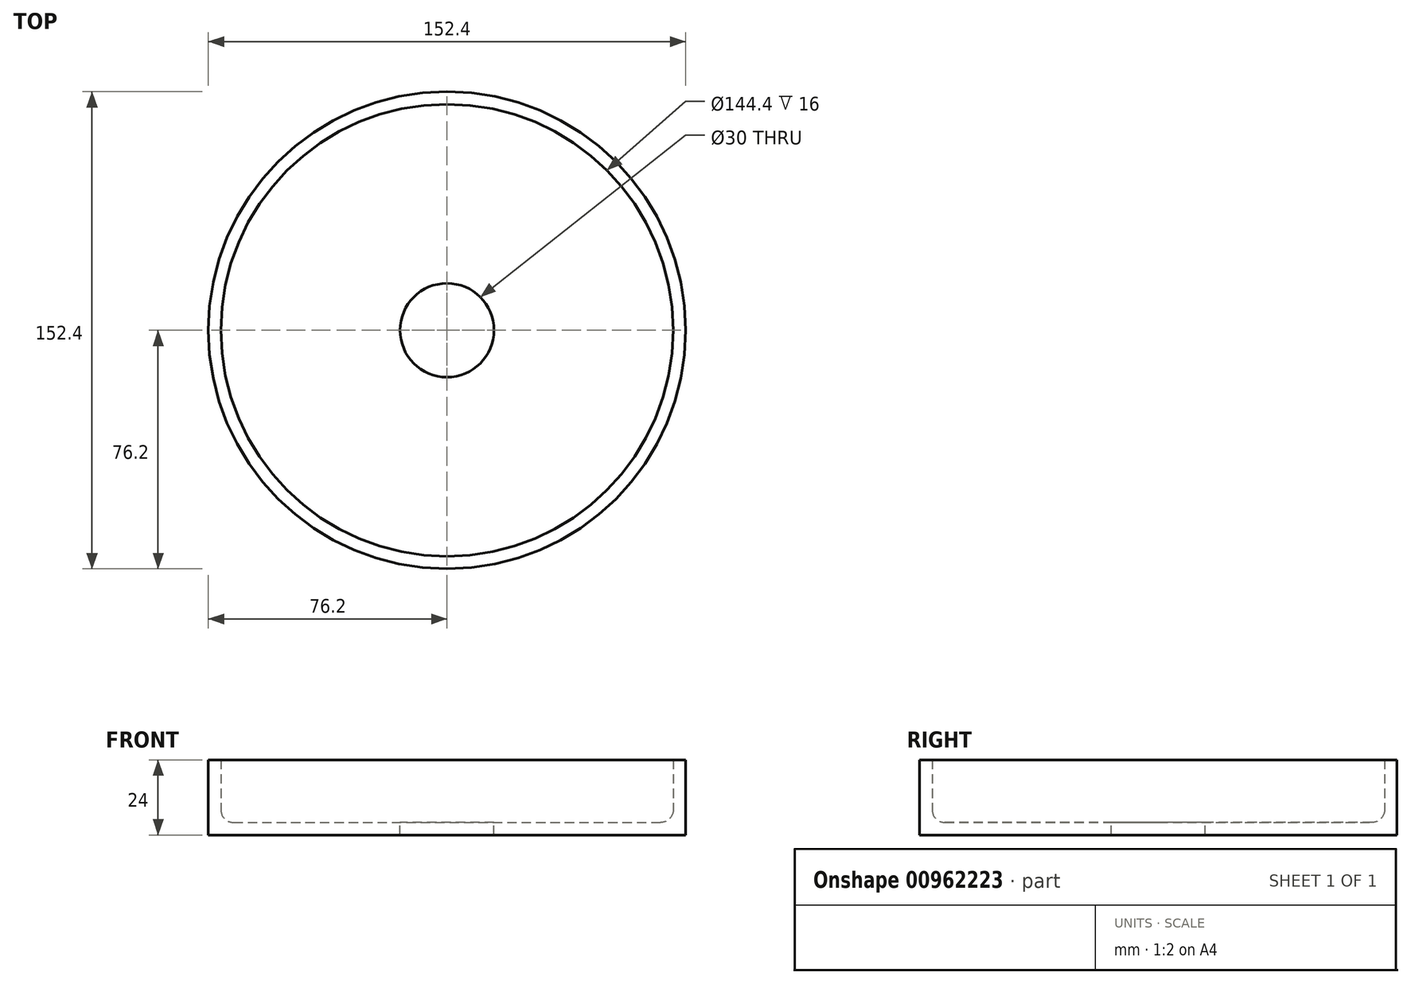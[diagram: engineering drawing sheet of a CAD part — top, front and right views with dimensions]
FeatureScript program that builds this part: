
annotation { "Feature Type Name" : "Feature", "Feature Type Description" : "" }
export const myFeature = defineFeature(function(context is Context, id is Id, definition is map)
    precondition{}
    {
        {
            var Q0;
            Q0=qCreatedBy(makeId("Front.planeOp"),FACE);
            var sketch = newSketch(context, id + "F0", { "sketchPlane" : qUnion([Q0])});
            skLineSegment(sketch, "E0", {"start": v(0, 0) * mm, "end": v(0, 4) * mm});
            skLineSegment(sketch, "E1.bottom", {"start": v(0, 0) * mm, "end": v(76.2, 0) * mm});
            skLineSegment(sketch, "E1.top", {"start": v(0, 4) * mm, "end": v(68.2, 4) * mm});
            skLineSegment(sketch, "E1.right", {"start": v(76.2, 0) * mm, "end": v(76.2, 4) * mm});
            skLineSegment(sketch, "E2.0", {"start": v(72.2, 0) * mm, "end": v(72.2, 3) * mm});
            skLineSegment(sketch, "E3.0", {"start": v(0, 20) * mm, "end": v(33.38, 20) * mm});
            skPoint(sketch, "E4.oppositeSnap0", {"position": v(72.2, 1.5) * mm});
            skLineSegment(sketch, "E4.bottom", {"start": v(76.2, 4) * mm, "end": v(72.2, 4) * mm});
            skLineSegment(sketch, "E4.top", {"start": v(76.2, 24) * mm, "end": v(72.2, 24) * mm});
            skLineSegment(sketch, "E4.left", {"start": v(76.2, 4) * mm, "end": v(76.2, 24) * mm});
            skLineSegment(sketch, "E4.right", {"start": v(72.2, 8) * mm, "end": v(72.2, 24) * mm});
            skPoint(sketch, "E5.newPointB", {"position": v(76.2, 4) * mm});
            skArc(sketch, "E5.filletArc", {"start": v(68.2, 4) * mm, "mid": v(71.03, 5.17) * mm, "end": v(72.2, 8) * mm});
            skSolve(sketch);
        }
        {
            var Q0;
            Q0=makeQuery(id+"F0.imprint","IMPRINT",FACE,{"disambiguationData":[TD([[makeQuery(id+"F0.imprint","IMPRINT",EDGE,{"derivedFrom":sQuery(id+"F0.wireOp",EDGE,"E1.top")}),-1.0]])]});
            var Q1;
            Q1=sQuery(id+"F0.wireOp",EDGE,"E0");
            revolve(context, id + "F1", {"surfaceOperationType" : NewSurfaceOperationType.NEW, "entities" : qUnion([Q0]), "axis" : qUnion([Q1]), "revolveType" : RevolveType.FULL});
        }
        {
            var Q0;
            Q0=makeQuery(id+"F1.opRevolve","SWEPT_FACE",FACE,{"disambiguationData":[OSD([sQuery(id+"F0.wireOp",EDGE,"E1.top")])]});
            var sketch = newSketch(context, id + "F2", { "sketchPlane" : qUnion([Q0])});
            skCircle(sketch, "E6", {"center": v(0, 0) * mm, "radius": 15 * mm});
            skSolve(sketch);
        }
        {
            var Q0;
            Q0 = qSketchRegion(id + "F2", true);
            extrude(context, id + "F3", {"entities" : qUnion([Q0]), "operationType" : NewBodyOperationType.REMOVE, "oppositeDirection" : true, "depth" : 25 * mm, "offsetDistance" : 25 * mm});
        }
    });
